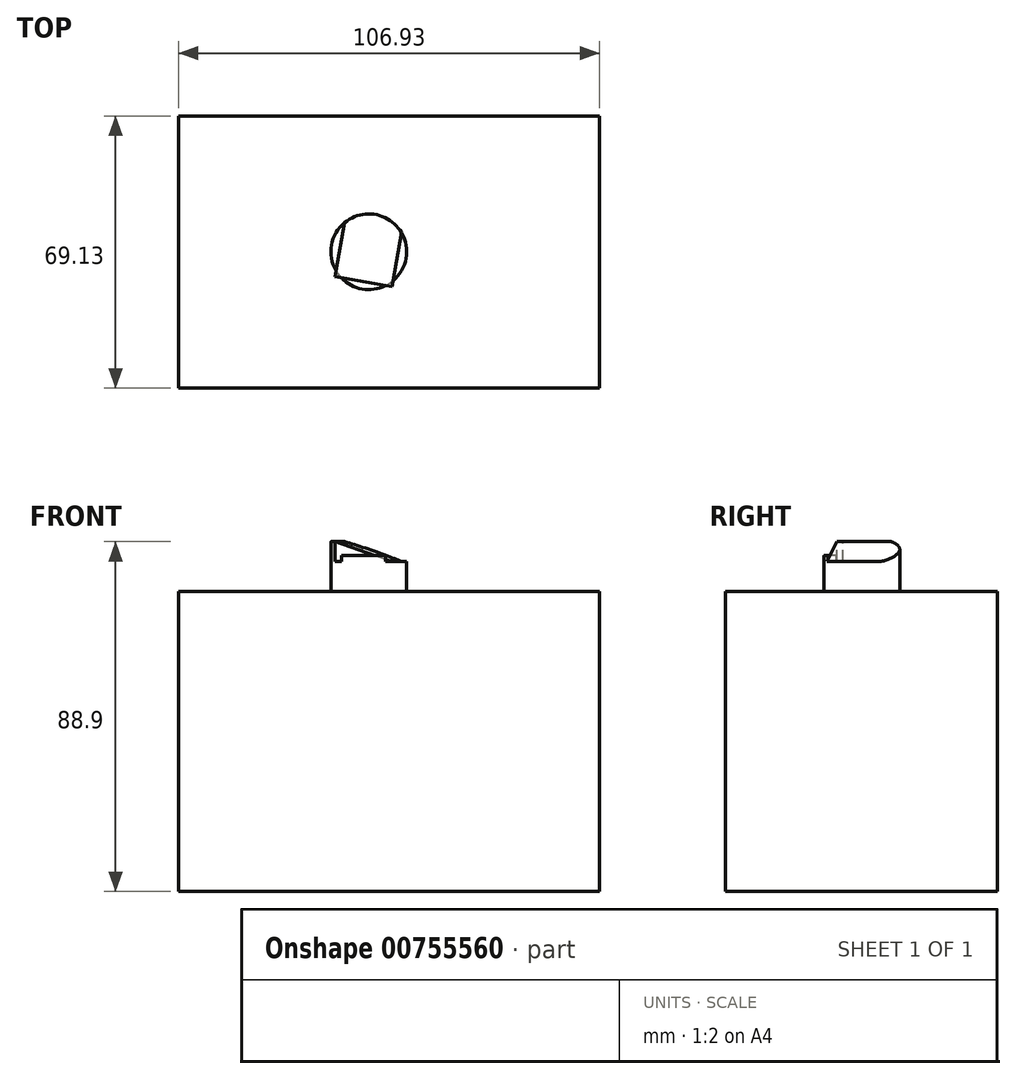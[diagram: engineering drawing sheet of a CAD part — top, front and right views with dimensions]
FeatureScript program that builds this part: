
annotation { "Feature Type Name" : "Feature", "Feature Type Description" : "" }
export const myFeature = defineFeature(function(context is Context, id is Id, definition is map)
    precondition{}
    {
        {
            var Q0;
            Q0=qCreatedBy(makeId("Top.planeOp"),FACE);
            var sketch = newSketch(context, id + "F0", { "sketchPlane" : qUnion([Q0])});
            skLineSegment(sketch, "E0", {"start": v(-50.24, 27.93) * mm, "end": v(-50.24, -41.2) * mm});
            skLineSegment(sketch, "E1", {"start": v(-50.24, -41.2) * mm, "end": v(56.7, -41.2) * mm});
            skLineSegment(sketch, "E2", {"start": v(56.7, -41.2) * mm, "end": v(56.7, 27.93) * mm});
            skLineSegment(sketch, "E3", {"start": v(56.7, 27.93) * mm, "end": v(-50.24, 27.93) * mm});
            skSolve(sketch);
        }
        {
            var Q0;
            Q0=makeQuery(id+"F0.imprint","IMPRINT",FACE,{"disambiguationData":[TD([[makeQuery(id+"F0.imprint","IMPRINT",EDGE,{"derivedFrom":sQuery(id+"F0.wireOp",EDGE,"E0")}),1.0]])]});
            extrude(context, id + "F1", {"entities" : qUnion([Q0]), "depth" : 76.2 * mm, "offsetDistance" : 25.4 * mm});
        }
        {
            var Q0;
            Q0=makeQuery(id+"F1.opExtrude","CAP_FACE",FACE,{"disambiguationData":[OSD([sQuery(id+"F0.wireOp",EDGE,"E0"),sQuery(id+"F0.wireOp",EDGE,"E1"),sQuery(id+"F0.wireOp",EDGE,"E2"),sQuery(id+"F0.wireOp",EDGE,"E3")])],"isStart":false});
            var sketch = newSketch(context, id + "F2", { "sketchPlane" : qUnion([Q0])});
            skCircle(sketch, "E4", {"center": v(-1.94, -6.54) * mm, "radius": 9.61 * mm});
            skSolve(sketch);
        }
        {
            var Q0;
            Q0=makeQuery(id+"F2.imprint","IMPRINT",FACE,{"disambiguationData":[TD([[makeQuery(id+"F2.imprint","IMPRINT",EDGE,{"derivedFrom":sQuery(id+"F2.wireOp",EDGE,"E4")}),1.0]])]});
            extrude(context, id + "F3", {"entities" : qUnion([Q0]), "operationType" : NewBodyOperationType.ADD, "depth" : 38.1 * mm, "offsetDistance" : 25.4 * mm});
        }
        {
            var Q0;
            Q0=makeQuery(id+"F3.opExtrude","CAP_FACE",FACE,{"disambiguationData":[OSD([sQuery(id+"F2.wireOp",EDGE,"E4")])],"isStart":false});
            var sketch = newSketch(context, id + "F4", { "sketchPlane" : qUnion([Q0])});
            skLineSegment(sketch, "E5", {"start": v(-11.93, -41.2) * mm, "end": v(-9.1, -12.95) * mm});
            skLineSegment(sketch, "E6", {"start": v(-9.1, -12.95) * mm, "end": v(10.14, -31.35) * mm});
            skLineSegment(sketch, "E7", {"start": v(10.14, -31.35) * mm, "end": v(10.14, -55.5) * mm});
            skLineSegment(sketch, "E8", {"start": v(10.14, -55.5) * mm, "end": v(-11.93, -41.2) * mm});
            skSolve(sketch);
        }
        {
            var Q0;
            {var subQ4=sQuery(id+"F4.wireOp",EDGE,"E5");Q0=makeQuery(id+"F4.imprint","IMPRINT",FACE,{"disambiguationData":[TD([[makeQuery(id+"F4.imprint","IMPRINT",EDGE,{"derivedFrom":subQ4}),-1.0]])]});}
            var Q1;
            {var subQ0=sQuery(id+"F4.wireOp",EDGE,"E6");var subQ1=makeQuery(id+"F3.opExtrude","CAP_EDGE",EDGE,{"disambiguationData":[OSD([sQuery(id+"F2.wireOp",EDGE,"E4")])],"isStart":false});var subQ3=makeQuery(id+"F4.imprint","INTERSECT",VERTEX,{"derivedFrom":[subQ1,subQ0]});Q1=makeQuery(id+"F4.imprint","IMPRINT",FACE,{"disambiguationData":[TD([[makeQuery(id+"F4.imprint","IMPRINT",EDGE,{"disambiguationData":[TD([[subQ3,1.0]])],"derivedFrom":subQ0}),1.0]])]});}
            extrude(context, id + "F5", {"entities" : qUnion([Q0, Q1]), "operationType" : NewBodyOperationType.REMOVE, "oppositeDirection" : true, "depth" : 25.4 * mm, "offsetDistance" : 25.4 * mm});
        }
        {
            var Q0;
            {var subQ0=sQuery(id+"F4.wireOp",EDGE,"E6");var subQ1=makeQuery(id+"F3.opExtrude","CAP_EDGE",EDGE,{"disambiguationData":[OSD([sQuery(id+"F2.wireOp",EDGE,"E4")])],"isStart":false});Q0=makeQuery(id+"F5.boolean.opBoolean","COPY",FACE,{"derivedFrom":makeQuery(id+"F5.opExtrude","SWEPT_FACE",FACE,{"disambiguationData":[OSD([subQ0]),TDD([makeQuery(id+"F4.imprint","IMPRINT",EDGE,{"disambiguationData":[TD([[makeQuery(id+"F4.imprint","INTERSECT",VERTEX,{"derivedFrom":[subQ1,subQ0]}),1.0]])],"derivedFrom":subQ0})])]})});}
            extrude(context, id + "F6", {"entities" : qUnion([Q0]), "operationType" : NewBodyOperationType.REMOVE, "oppositeDirection" : true, "depth" : 25.4 * mm, "offsetDistance" : 25.4 * mm});
        }
        {
            var Q0;
            {var subQ0=sQuery(id+"F4.wireOp",EDGE,"E6");var subQ1=sQuery(id+"F2.wireOp",EDGE,"E4");var subQ2=makeQuery(id+"F3.opExtrude","CAP_EDGE",EDGE,{"disambiguationData":[OSD([subQ1])],"isStart":false});Q0=makeQuery(id+"F6.boolean.opBoolean","MERGE",FACE,{"derivedFrom":[makeQuery(id+"F5.boolean.opBoolean","COPY",FACE,{"derivedFrom":makeQuery(id+"F5.opExtrude","CAP_FACE",FACE,{"disambiguationData":[OSD([subQ1,subQ0])],"isStart":false})}),makeQuery(id+"F6.opExtrude","SWEPT_FACE",FACE,{"disambiguationData":[OSD([subQ0]),TDD([makeQuery(id+"F5.boolean.opBoolean","COPY",EDGE,{"derivedFrom":makeQuery(id+"F5.opExtrude","CAP_EDGE",EDGE,{"disambiguationData":[OSD([subQ0]),TDD([makeQuery(id+"F4.imprint","IMPRINT",EDGE,{"disambiguationData":[TD([[makeQuery(id+"F4.imprint","INTERSECT",VERTEX,{"derivedFrom":[subQ2,subQ0]}),1.0]])],"derivedFrom":subQ0})])],"isStart":false})})])]})]});}
            var sketch = newSketch(context, id + "F7", { "sketchPlane" : qUnion([Q0])});
            skLineSegment(sketch, "E9", {"start": v(-10.25, -11.38) * mm, "end": v(4.19, -13.96) * mm});
            skSolve(sketch);
        }
        {
            var Q0;
            {var subQ0=sQuery(id+"F7.wireOp",EDGE,"E9");Q0=makeQuery(id+"F7.imprint","IMPRINT",FACE,{"disambiguationData":[TD([[makeQuery(id+"F7.imprint","IMPRINT",EDGE,{"derivedFrom":subQ0}),-1.0]])]});}
            extrude(context, id + "F8", {"entities" : qUnion([Q0]), "operationType" : NewBodyOperationType.REMOVE, "oppositeDirection" : true, "depth" : 5.08 * mm, "offsetDistance" : 25.4 * mm});
        }
        {
            var Q0;
            Q0=makeQuery(id+"F8.boolean.opBoolean","COPY",FACE,{"derivedFrom":makeQuery(id+"F8.opExtrude","SWEPT_FACE",FACE,{"disambiguationData":[OSD([sQuery(id+"F7.wireOp",EDGE,"E9")])]})});
            var sketch = newSketch(context, id + "F9", { "sketchPlane" : qUnion([Q0])});
            skLineSegment(sketch, "E10", {"start": v(6.58, 83.82) * mm, "end": v(-8.08, 88.9) * mm});
            skLineSegment(sketch, "E11", {"start": v(-8.08, 88.9) * mm, "end": v(6.58, 88.9) * mm});
            skLineSegment(sketch, "E12", {"start": v(6.58, 88.9) * mm, "end": v(6.58, 83.82) * mm});
            skSolve(sketch);
        }
        {
            var Q0;
            Q0=makeQuery(id+"F9.imprint","IMPRINT",FACE,{"disambiguationData":[TD([[makeQuery(id+"F9.imprint","IMPRINT",EDGE,{"derivedFrom":sQuery(id+"F9.wireOp",EDGE,"E10")}),-1.0]])]});
            extrude(context, id + "F10", {"entities" : qUnion([Q0]), "operationType" : NewBodyOperationType.REMOVE, "oppositeDirection" : true, "depth" : 25.4 * mm, "offsetDistance" : 25.4 * mm});
        }
        {
            var Q0;
            {var subQ0=sQuery(id+"F2.wireOp",EDGE,"E4");var subQ1=sQuery(id+"F4.wireOp",EDGE,"E6");var subQ2=makeQuery(id+"F3.opExtrude","CAP_EDGE",EDGE,{"disambiguationData":[OSD([subQ0])],"isStart":false});Q0=makeQuery(id+"F10.boolean.opBoolean","SPLIT",FACE,{"disambiguationData":[TD([makeQuery(id+"F10.opExtrude","SWEPT_FACE",FACE,{"disambiguationData":[OSD([sQuery(id+"F9.wireOp",EDGE,"E12")])]})])],"derivedFrom":makeQuery(id+"F6.boolean.opBoolean","MERGE",FACE,{"derivedFrom":[makeQuery(id+"F5.boolean.opBoolean","COPY",FACE,{"derivedFrom":makeQuery(id+"F5.opExtrude","CAP_FACE",FACE,{"disambiguationData":[OSD([subQ0,subQ1])],"isStart":false})}),makeQuery(id+"F6.opExtrude","SWEPT_FACE",FACE,{"disambiguationData":[OSD([subQ1]),TDD([makeQuery(id+"F5.boolean.opBoolean","COPY",EDGE,{"derivedFrom":makeQuery(id+"F5.opExtrude","CAP_EDGE",EDGE,{"disambiguationData":[OSD([subQ1]),TDD([makeQuery(id+"F4.imprint","IMPRINT",EDGE,{"disambiguationData":[TD([[makeQuery(id+"F4.imprint","INTERSECT",VERTEX,{"derivedFrom":[subQ2,subQ1]}),1.0]])],"derivedFrom":subQ1})])],"isStart":false})})])]})]})});}
            extrude(context, id + "F11", {"entities" : qUnion([Q0]), "operationType" : NewBodyOperationType.REMOVE, "oppositeDirection" : true, "depth" : 5.08 * mm, "offsetDistance" : 25.4 * mm});
        }
        {
            var Q0;
            Q0=makeQuery(id+"F8.boolean.opBoolean","COPY",FACE,{"derivedFrom":makeQuery(id+"F8.opExtrude","SWEPT_FACE",FACE,{"disambiguationData":[OSD([sQuery(id+"F7.wireOp",EDGE,"E9")])]})});
            extrude(context, id + "F12", {"entities" : qUnion([Q0]), "operationType" : NewBodyOperationType.ADD, "depth" : 1.52 * mm, "offsetDistance" : 25.4 * mm});
        }
        {
            var Q0;
            Q0=makeQuery(id+"F8.boolean.opBoolean","COPY",FACE,{"derivedFrom":makeQuery(id+"F8.opExtrude","CAP_FACE",FACE,{"disambiguationData":[OSD([sQuery(id+"F2.wireOp",EDGE,"E4"),sQuery(id+"F4.wireOp",EDGE,"E6"),sQuery(id+"F7.wireOp",EDGE,"E9")])],"isStart":false})});
            extrude(context, id + "F13", {"entities" : qUnion([Q0]), "operationType" : NewBodyOperationType.ADD, "depth" : 1.52 * mm, "offsetDistance" : 25.4 * mm});
        }
    });
